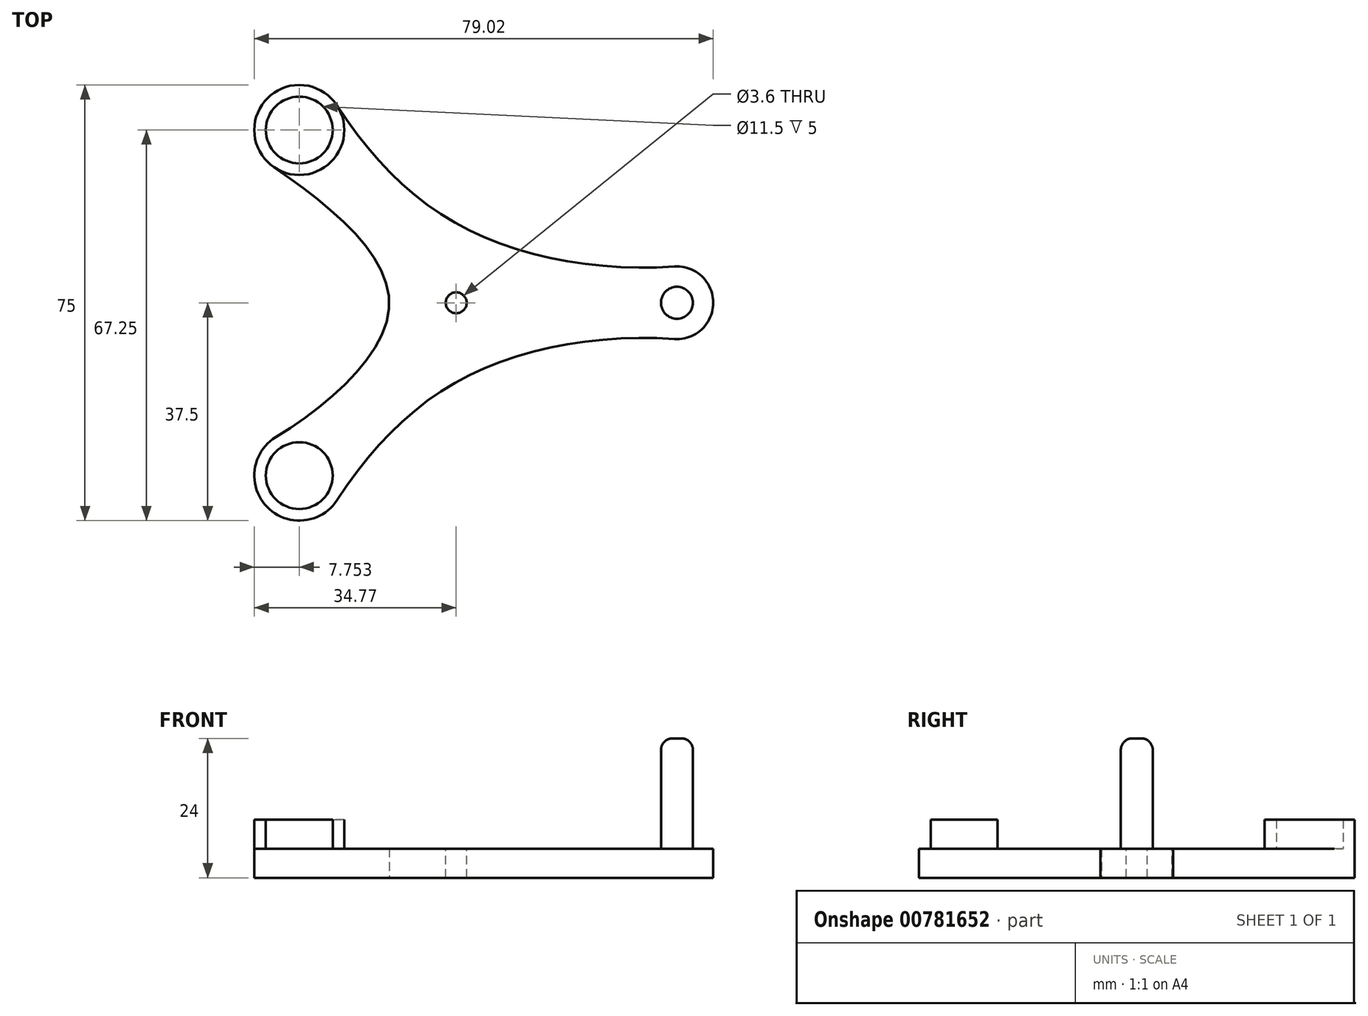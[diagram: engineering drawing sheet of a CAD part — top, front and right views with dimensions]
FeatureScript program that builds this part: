
annotation { "Feature Type Name" : "Feature", "Feature Type Description" : "" }
export const myFeature = defineFeature(function(context is Context, id is Id, definition is map)
    precondition{}
    {
        {
            var Q0;
            Q0=qCreatedBy(makeId("Top.planeOp"),FACE);
            var sketch = newSketch(context, id + "F0", { "sketchPlane" : qUnion([Q0])});
            skLineSegment(sketch, "E0", {"start": v(-46.84, 0) * mm, "end": v(80.45, 0) * mm, "construction": true});
            skLineSegment(sketch, "E1", {"start": v(45.75, 37.45) * mm, "end": v(45.75, -68.52) * mm, "construction": true});
            skCircle(sketch, "E2", {"center": v(-27.02, 29.75) * mm, "radius": 5.25 * mm, "construction": true});
            skCircle(sketch, "E3.MirrorC", {"center": v(-27.02, -29.75) * mm, "radius": 5.25 * mm, "construction": true});
            skCircle(sketch, "E4", {"center": v(38, 0) * mm, "radius": 6.25 * mm, "construction": true});
            skCircle(sketch, "E5", {"center": v(-27.02, 29.75) * mm, "radius": 5.75 * mm});
            skCircle(sketch, "E6", {"center": v(38, 0) * mm, "radius": 3.25 * mm, "construction": true});
            skCircle(sketch, "E7", {"center": v(-27.02, 29.75) * mm, "radius": 7.75 * mm});
            skCircle(sketch, "E8.MirrorC", {"center": v(-27.02, -29.75) * mm, "radius": 5.75 * mm});
            skCircle(sketch, "E9.MirrorC", {"center": v(-27.02, -29.75) * mm, "radius": 7.75 * mm});
            skCircle(sketch, "E10", {"center": v(38, 0) * mm, "radius": 2.75 * mm});
            skPoint(sketch, "E11", {"position": v(45.75, 0) * mm});
            skLineSegment(sketch, "E12", {"start": v(45.75, 20) * mm, "end": v(45.75, -20) * mm, "construction": true});
            skArc(sketch, "E13", {"start": v(45.75, 20) * mm, "mid": v(59.45, 0) * mm, "end": v(45.75, -20) * mm, "construction": true});
            skFitSpline(sketch, "E14", {"points": [v(-20.53, 33.99) * mm, v(2.8, 12.2) * mm, v(37.59, 6.24) * mm], "startDerivative": vector(38.93, -59.6) * mm, "endDerivative": vector(70.23, 4.65) * mm});
            skFitSpline(sketch, "E15.MirrorCS", {"points": [v(-20.53, -33.99) * mm, v(2.8, -12.2) * mm, v(37.59, -6.24) * mm], "startDerivative": vector(38.93, 59.6) * mm, "endDerivative": vector(70.23, -4.65) * mm});
            skArc(sketch, "E16", {"start": v(37.59, 6.24) * mm, "mid": v(44.25, 0) * mm, "end": v(37.59, -6.24) * mm});
            skFitSpline(sketch, "E17", {"points": [v(-31.4, 23.35) * mm, v(-11.54, 0) * mm, v(-31.08, -23.15) * mm], "startDerivative": vector(58.02, -39.7) * mm, "endDerivative": vector(-57.84, -35.56) * mm});
            skCircle(sketch, "E18", {"center": v(0, 0) * mm, "radius": 1.8 * mm});
            skSolve(sketch);
        }
        {
            var Q0;
            Q0=makeQuery(id+"F0.imprint","IMPRINT",FACE,{"disambiguationData":[TD([[makeQuery(id+"F0.imprint","IMPRINT",EDGE,{"derivedFrom":sQuery(id+"F0.wireOp",EDGE,"E10")}),-1.0]])]});
            var Q1;
            Q1=makeQuery(id+"F0.imprint","IMPRINT",FACE,{"disambiguationData":[TD([[makeQuery(id+"F0.imprint","IMPRINT",EDGE,{"derivedFrom":sQuery(id+"F0.wireOp",EDGE,"E5")}),-1.0]])]});
            var Q2;
            Q2=makeQuery(id+"F0.imprint","IMPRINT",FACE,{"disambiguationData":[TD([[makeQuery(id+"F0.imprint","IMPRINT",EDGE,{"derivedFrom":sQuery(id+"F0.wireOp",EDGE,"E5")}),1.0]])]});
            var Q3;
            Q3=makeQuery(id+"F0.imprint","IMPRINT",FACE,{"disambiguationData":[TD([[makeQuery(id+"F0.imprint","IMPRINT",EDGE,{"derivedFrom":sQuery(id+"F0.wireOp",EDGE,"E8.MirrorC")}),1.0]])]});
            var Q4;
            Q4=makeQuery(id+"F0.imprint","IMPRINT",FACE,{"disambiguationData":[TD([[makeQuery(id+"F0.imprint","IMPRINT",EDGE,{"derivedFrom":sQuery(id+"F0.wireOp",EDGE,"E8.MirrorC")}),-1.0]])]});
            var Q5;
            Q5=makeQuery(id+"F0.imprint","IMPRINT",FACE,{"disambiguationData":[TD([[makeQuery(id+"F0.imprint","IMPRINT",EDGE,{"derivedFrom":sQuery(id+"F0.wireOp",EDGE,"E10")}),1.0]])]});
            extrude(context, id + "F1", {"entities" : qUnion([Q0, Q1, Q2, Q3, Q4, Q5]), "oppositeDirection" : true, "depth" : 5 * mm, "offsetDistance" : 25 * mm});
        }
        {
            var Q0;
            Q0=makeQuery(id+"F0.imprint","IMPRINT",FACE,{"disambiguationData":[TD([[makeQuery(id+"F0.imprint","IMPRINT",EDGE,{"derivedFrom":sQuery(id+"F0.wireOp",EDGE,"E5")}),-1.0]])]});
            var Q1;
            Q1=makeQuery(id+"F0.imprint","IMPRINT",FACE,{"disambiguationData":[TD([[makeQuery(id+"F0.imprint","IMPRINT",EDGE,{"derivedFrom":sQuery(id+"F0.wireOp",EDGE,"E8.MirrorC")}),1.0]])]});
            extrude(context, id + "F2", {"entities" : qUnion([Q0, Q1]), "operationType" : NewBodyOperationType.ADD, "depth" : 5 * mm, "offsetDistance" : 25 * mm});
        }
        {
            var Q0;
            Q0=makeQuery(id+"F0.imprint","IMPRINT",FACE,{"disambiguationData":[TD([[makeQuery(id+"F0.imprint","IMPRINT",EDGE,{"derivedFrom":sQuery(id+"F0.wireOp",EDGE,"E10")}),1.0]])]});
            extrude(context, id + "F3", {"entities" : qUnion([Q0]), "operationType" : NewBodyOperationType.ADD, "depth" : 19 * mm, "offsetDistance" : 25 * mm});
        }
        {
            var Q0;
            Q0=makeQuery(id+"F3.opExtrude","CAP_EDGE",EDGE,{"disambiguationData":[OSD([sQuery(id+"F0.wireOp",EDGE,"E10")])],"isStart":false});
            fillet(context, id + "F4", {"entities" : qUnion([Q0]), "radius" : 2 * mm, "tangentPropagation" : true, "allowEdgeOverflow" : false});
        }
    });
